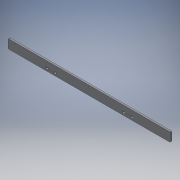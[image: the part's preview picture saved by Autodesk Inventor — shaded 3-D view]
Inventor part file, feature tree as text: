
AUTODESK INVENTOR PART (.ipt)
format: ipt  version: 2019 (Build 230136000, 136)  size: 159,744 bytes
history: native  units: mm
features: reference x12, extrude x2, sketch x2, other x2, fillet x1, helix x1
ambient origin geometry x8: Origin, YZ Plane, XZ Plane, XY Plane, X Axis, Y Axis, Z Axis, Center Point
bodies: Solid1 (feature_tree)
feature tree (20):
  extrude  "Extrusion1"  Depth=15.0mm
  fillet  "Fillet1"  Radius=0.2mm
  extrude  "Extrusion2"  Depth=4.0mm
  sketch  "Sketch1"  dims[d0=5.0mm d1=15.0mm d2=0.2mm]
  reference  "Reference1"
  reference  "Reference2"
  reference  "Reference3"
  reference  "Reference4"
  reference  "Reference5"
  reference  "Reference6"
  reference  "Reference7"
  reference  "Reference8"
  reference  "Reference9"
  reference  "Reference10"
  reference  "Reference11"
  reference  "Reference12"
  sketch  "Sketch2"  dims[d3=0.2mm d4=0.2mm d5=0.2mm d6=3.2mm d7=3.2mm d8=4.0mm d9=0.0mm d10=2.0mm d11=4.0mm d12=4.0mm d13=4.0mm d14=20.0mm d15=20.0mm d16=8.0mm d17=8.0mm d18=8.0mm d19=4.0mm d20=0.0mm]
  other  "<userpath>\Documents\CAD Files\Helix DLP\Helix DLP.iam"
  helix  "Helix DLP.iam"  [1 undecoded]
  other  "Wiper_Arm_1:1"
note: 1 required parameter value undecoded (feature->parameter linkage not recoverable at this tier; creation-order binding heuristic only, values carry confidence <= 0.55)
